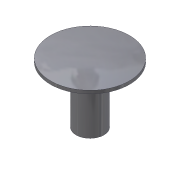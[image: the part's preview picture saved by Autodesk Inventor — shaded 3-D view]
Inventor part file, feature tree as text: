
AUTODESK INVENTOR PART (.ipt)
format: ipt  version: 2014 SP1 (Build 180222100, 222)  size: 92,160 bytes
history: native  units: mm (DEFAULTED — no unit token found)
features: sketch x2, reference x2, revolve x1, extrude x1
ambient origin geometry x8: Origin, YZ Plane, XZ Plane, XY Plane, X Axis, Y Axis, Z Axis, Center Point
bodies: Solid1 (feature_tree)
feature tree (6):
  revolve  "Revolution1"  [1 undecoded]
  extrude  "Extrusion1"  [1 undecoded]
  sketch  "Sketch1"  dims[d0=90.0deg d1=3.175mm d2=0.0mm]
  reference  "Reference1"
  reference  "Reference2"
  sketch  "Sketch2"
note: 2 required parameter values undecoded (feature->parameter linkage not recoverable at this tier; creation-order binding heuristic only, values carry confidence <= 0.55)